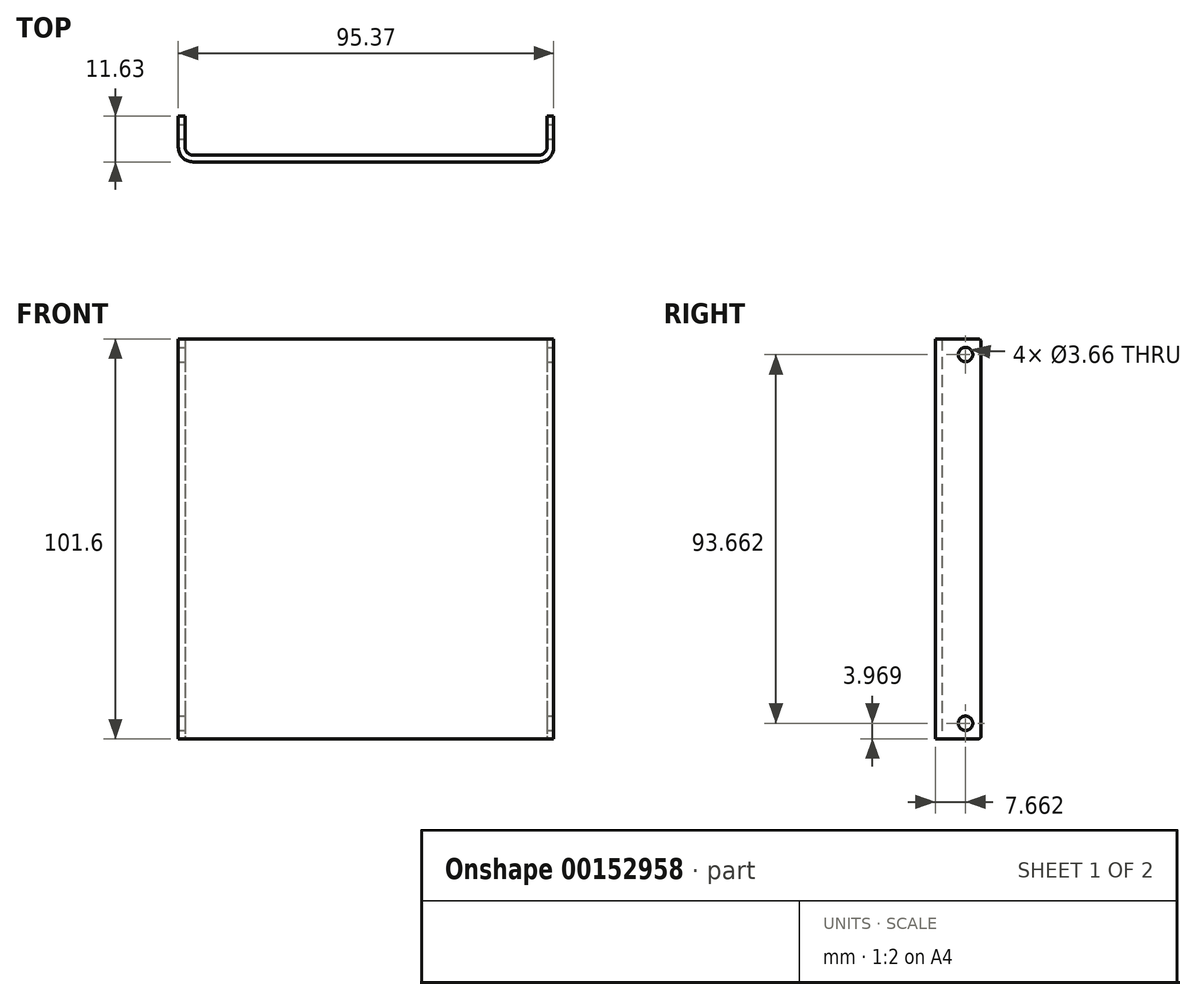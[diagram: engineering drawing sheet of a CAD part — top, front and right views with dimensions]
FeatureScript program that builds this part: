
annotation { "Feature Type Name" : "Feature", "Feature Type Description" : "" }
export const myFeature = defineFeature(function(context is Context, id is Id, definition is map)
    precondition{}
    {
        {
            var Q0;
            Q0=qCreatedBy(makeId("Top.planeOp"),FACE);
            var sketch = newSketch(context, id + "F0", { "sketchPlane" : qUnion([Q0])});
            skLineSegment(sketch, "E0.bottom", {"start": v(0, 0) * mm, "end": v(-91.95, 0) * mm});
            skLineSegment(sketch, "E0.top", {"start": v(1.7, -1.7) * mm, "end": v(-93.66, -1.7) * mm});
            skLineSegment(sketch, "E1.top", {"start": v(-91.95, 9.92) * mm, "end": v(-93.66, 9.92) * mm});
            skLineSegment(sketch, "E1.left", {"start": v(-91.95, 0) * mm, "end": v(-91.95, 9.92) * mm});
            skLineSegment(sketch, "E1.right", {"start": v(-93.66, -1.7) * mm, "end": v(-93.66, 9.92) * mm});
            skLineSegment(sketch, "E2.top", {"start": v(0, 9.92) * mm, "end": v(1.7, 9.92) * mm});
            skLineSegment(sketch, "E2.left", {"start": v(0, 0) * mm, "end": v(0, 9.92) * mm});
            skLineSegment(sketch, "E2.right", {"start": v(1.7, -1.7) * mm, "end": v(1.7, 9.92) * mm});
            skLineSegment(sketch, "E3", {"start": v(-45.98, 0) * mm, "end": v(-45.98, -1.7) * mm, "construction": true});
            skSolve(sketch);
        }
        {
            var Q0;
            Q0=qSketchRegion(id+"F0",true);
            extrude(context, id + "F1", {"entities" : qUnion([Q0]), "depth" : 101.6 * mm});
        }
        {
            var Q0;
            Q0=makeQuery(id+"F1.opExtrude","SWEPT_EDGE",EDGE,{"disambiguationData":[OSD([sQuery(id+"F0.wireOp",EDGE,"E0.top"),sQuery(id+"F0.wireOp",EDGE,"E2.right")])]});
            var Q1;
            Q1=makeQuery(id+"F1.opExtrude","SWEPT_EDGE",EDGE,{"disambiguationData":[OSD([sQuery(id+"F0.wireOp",EDGE,"E0.top"),sQuery(id+"F0.wireOp",EDGE,"E1.right")])]});
            var Q2;
            Q2=makeQuery(id+"FqNnmMD7oaRdpTN_1.opExtrude","CAP_EDGE",EDGE,{"disambiguationData":[OSD([sQuery(id+"FY5sMr6MULj5lJw_1.wireOp",EDGE,"W42EfhJi-fDm4-L9BW-folL-irsYfDskuzBk.top")])],"isStart":false});
            fillet(context, id + "F2", {"entities" : qUnion([Q0, Q1, Q2]), "radius" : 3.7 * mm, "tangentPropagation" : true, "allowEdgeOverflow" : false});
        }
        {
            var Q0;
            Q0=makeQuery(id+"F1.opExtrude","SWEPT_EDGE",EDGE,{"disambiguationData":[OSD([sQuery(id+"F0.wireOp",EDGE,"E0.bottom"),sQuery(id+"F0.wireOp",EDGE,"E2.left")])]});
            var Q1;
            Q1=makeQuery(id+"F1.opExtrude","SWEPT_EDGE",EDGE,{"disambiguationData":[OSD([sQuery(id+"F0.wireOp",EDGE,"E0.bottom"),sQuery(id+"F0.wireOp",EDGE,"E1.left")])]});
            fillet(context, id + "F3", {"entities" : qUnion([Q0, Q1]), "radius" : 1.98 * mm, "tangentPropagation" : true, "allowEdgeOverflow" : false});
        }
        {
            var Q0;
            Q0=makeQuery(id+"F1.opExtrude","SWEPT_FACE",FACE,{"disambiguationData":[OSD([sQuery(id+"F0.wireOp",EDGE,"E2.right")])]});
            var sketch = newSketch(context, id + "F4", { "sketchPlane" : qUnion([Q0])});
            skLineSegment(sketch, "E4.bottom", {"start": v(5.95, 101.6) * mm, "end": v(9.92, 101.6) * mm, "construction": true});
            skLineSegment(sketch, "E4.top", {"start": v(5.95, 97.63) * mm, "end": v(9.92, 97.63) * mm, "construction": true});
            skLineSegment(sketch, "E4.left", {"start": v(5.95, 101.6) * mm, "end": v(5.95, 97.63) * mm, "construction": true});
            skLineSegment(sketch, "E4.right", {"start": v(9.92, 101.6) * mm, "end": v(9.92, 97.63) * mm, "construction": true});
            skLineSegment(sketch, "E5.bottom", {"start": v(5.95, 0) * mm, "end": v(9.92, 0) * mm, "construction": true});
            skLineSegment(sketch, "E5.top", {"start": v(5.95, 3.97) * mm, "end": v(9.92, 3.97) * mm, "construction": true});
            skLineSegment(sketch, "E5.left", {"start": v(5.95, 0) * mm, "end": v(5.95, 3.97) * mm, "construction": true});
            skLineSegment(sketch, "E5.right", {"start": v(9.92, 0) * mm, "end": v(9.92, 3.97) * mm, "construction": true});
            skCircle(sketch, "E6", {"center": v(5.95, 97.63) * mm, "radius": 1.83 * mm});
            skCircle(sketch, "E7", {"center": v(5.95, 3.97) * mm, "radius": 1.83 * mm});
            skSolve(sketch);
        }
        {
            var Q0;
            Q0=qSketchRegion(id+"F4",true);
            var Q1;
            Q1=makeQuery(id+"F1.opExtrude","SWEPT_FACE",FACE,{"disambiguationData":[OSD([sQuery(id+"F0.wireOp",EDGE,"E1.right")])]});
            extrude(context, id + "F5", {"entities" : qUnion([Q0]), "operationType" : NewBodyOperationType.REMOVE, "endBound" : BoundingType.UP_TO_SURFACE, "oppositeDirection" : true, "endBoundEntityFace" : qUnion([Q1]), "depth" : 25.4 * mm});
        }
        {
            var Q0;
            Q0=makeQuery(id+"F1.opExtrude","CAP_EDGE",EDGE,{"disambiguationData":[OSD([sQuery(id+"F0.wireOp",EDGE,"E1.top")])],"isStart":false});
            var Q1;
            Q1=makeQuery(id+"F1.opExtrude","CAP_EDGE",EDGE,{"disambiguationData":[OSD([sQuery(id+"F0.wireOp",EDGE,"E1.top")])],"isStart":true});
            var Q2;
            Q2=makeQuery(id+"F1.opExtrude","CAP_EDGE",EDGE,{"disambiguationData":[OSD([sQuery(id+"F0.wireOp",EDGE,"E2.top")])],"isStart":true});
            var Q3;
            Q3=makeQuery(id+"F1.opExtrude","CAP_EDGE",EDGE,{"disambiguationData":[OSD([sQuery(id+"F0.wireOp",EDGE,"E2.top")])],"isStart":false});
            fillet(context, id + "F6", {"entities" : qUnion([Q0, Q1, Q2, Q3]), "radius" : 0.76 * mm, "tangentPropagation" : true, "allowEdgeOverflow" : false});
        }
    });
